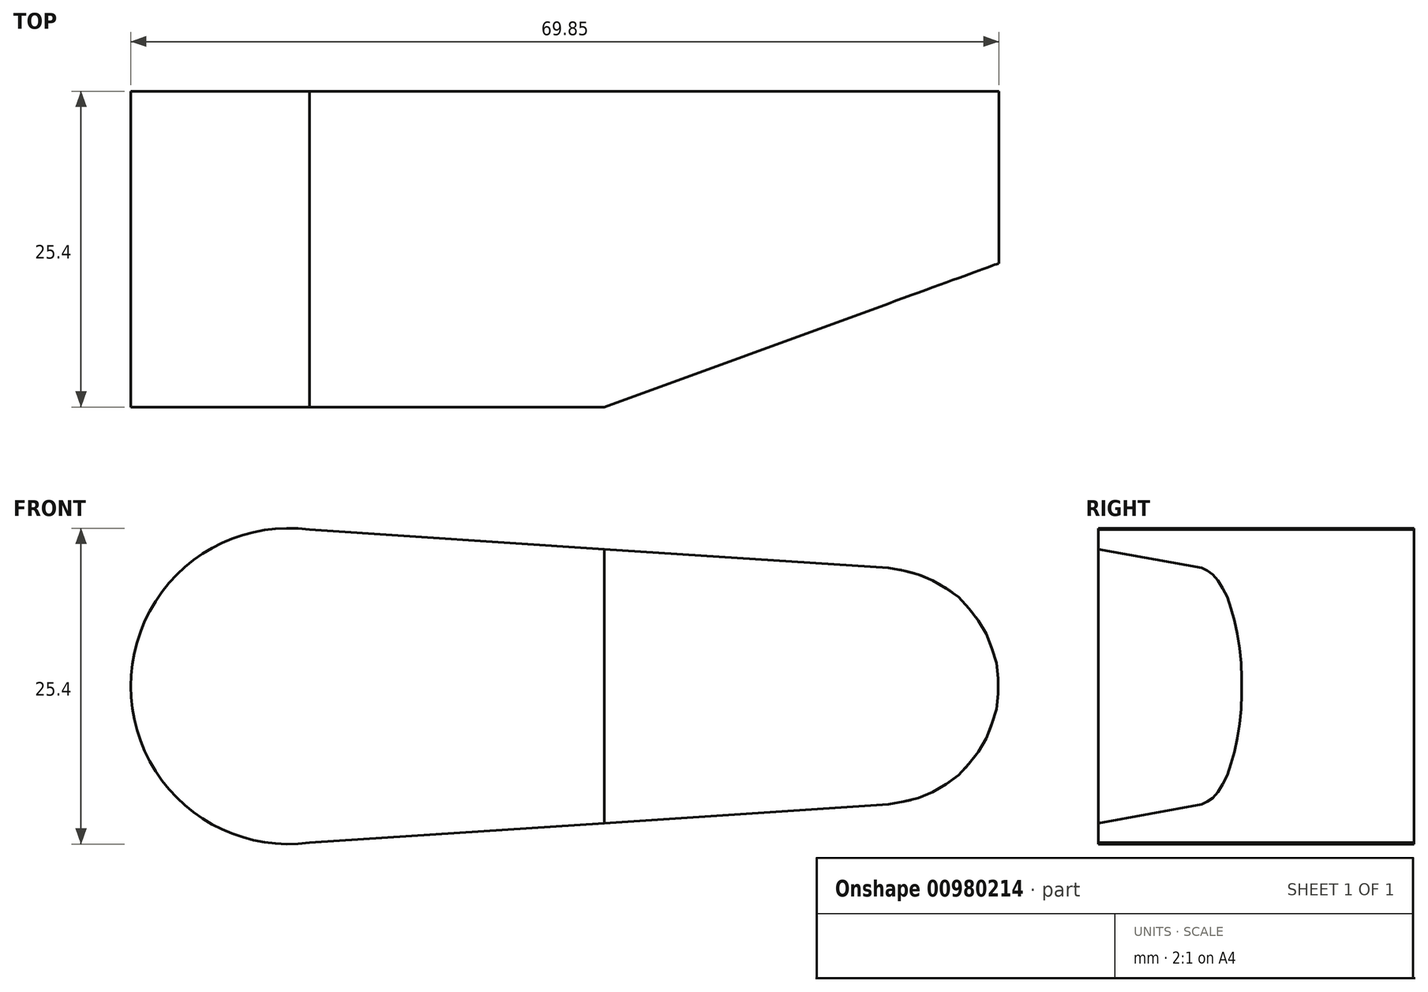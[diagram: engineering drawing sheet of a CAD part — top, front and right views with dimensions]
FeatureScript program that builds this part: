
annotation { "Feature Type Name" : "Feature", "Feature Type Description" : "" }
export const myFeature = defineFeature(function(context is Context, id is Id, definition is map)
    precondition{}
    {
        {
            var Q0;
            Q0=qCreatedBy(makeId("Front.planeOp"),FACE);
            var sketch = newSketch(context, id + "F0", { "sketchPlane" : qUnion([Q0])});
            skCircle(sketch, "E0", {"center": v(0, 0) * mm, "radius": 12.7 * mm});
            skCircle(sketch, "E1", {"center": v(47.62, 0) * mm, "radius": 9.53 * mm});
            skLineSegment(sketch, "E2", {"start": v(0, -12.7) * mm, "end": v(48.25, -9.5) * mm});
            skLineSegment(sketch, "E3", {"start": v(0, 12.7) * mm, "end": v(48.25, 9.5) * mm});
            skSolve(sketch);
        }
        {
            var Q0;
            Q0 = qSketchRegion(id + "F0", true);
            extrude(context, id + "F1", {"entities" : qUnion([Q0]), "oppositeDirection" : true, "depth" : 25.4 * mm, "offsetDistance" : 25.4 * mm});
        }
        {
            var Q0;
            Q0=qCreatedBy(makeId("Top.planeOp"),FACE);
            var sketch = newSketch(context, id + "F2", { "sketchPlane" : qUnion([Q0])});
            skLineSegment(sketch, "E4", {"start": v(57.15, 0) * mm, "end": v(25.4, 0) * mm});
            skLineSegment(sketch, "E5", {"start": v(25.4, 0) * mm, "end": v(57.15, 11.56) * mm});
            skLineSegment(sketch, "E6", {"start": v(57.15, 11.56) * mm, "end": v(57.15, 0) * mm});
            skLineSegment(sketch, "E7", {"start": v(57.15, 25.4) * mm, "end": v(57.15, 0) * mm});
            skSolve(sketch);
        }
        {
            var Q0;
            Q0=makeQuery(id+"F2.imprint","IMPRINT",FACE,{"disambiguationData":[TD([[makeQuery(id+"F2.imprint","IMPRINT",EDGE,{"derivedFrom":sQuery(id+"F2.wireOp",EDGE,"E4")}),-1.0]])]});
            extrude(context, id + "F3", {"entities" : qUnion([Q0]), "operationType" : NewBodyOperationType.REMOVE, "endBound" : BoundingType.SYMMETRIC, "depth" : 25.4 * mm, "offsetDistance" : 25.4 * mm});
        }
    });
